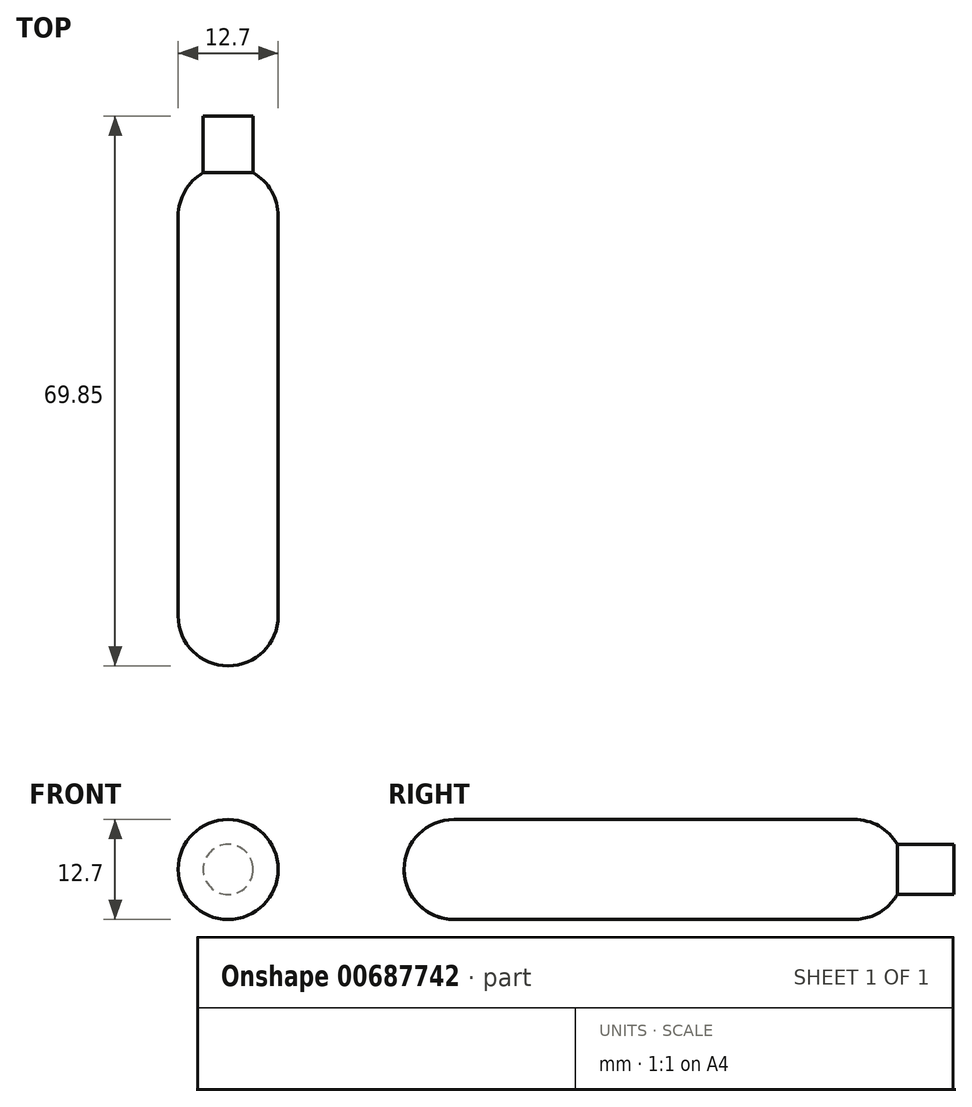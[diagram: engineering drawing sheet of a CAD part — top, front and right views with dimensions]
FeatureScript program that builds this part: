
annotation { "Feature Type Name" : "Feature", "Feature Type Description" : "" }
export const myFeature = defineFeature(function(context is Context, id is Id, definition is map)
    precondition{}
    {
        {
            var Q0;
            Q0=qCreatedBy(makeId("Front.planeOp"),FACE);
            var sketch = newSketch(context, id + "F0", { "sketchPlane" : qUnion([Q0])});
            skCircle(sketch, "E0", {"center": v(0, 0) * mm, "radius": 6.35 * mm});
            skSolve(sketch);
        }
        {
            var Q0;
            Q0=makeQuery(id+"F0.imprint","IMPRINT",FACE,{"disambiguationData":[TD([[makeQuery(id+"F0.imprint","IMPRINT",EDGE,{"derivedFrom":sQuery(id+"F0.wireOp",EDGE,"E0")}),1.0]])]});
            extrude(context, id + "F1", {"entities" : qUnion([Q0]), "depth" : 63.5 * mm, "offsetDistance" : 25.4 * mm});
        }
        {
            var Q0;
            Q0=makeQuery(id+"F1.opExtrude","CAP_FACE",FACE,{"disambiguationData":[OSD([sQuery(id+"F0.wireOp",EDGE,"E0")])],"isStart":false});
            var Q1;
            Q1=makeQuery(id+"F1.opExtrude","CAP_FACE",FACE,{"disambiguationData":[OSD([sQuery(id+"F0.wireOp",EDGE,"E0")])],"isStart":true});
            fillet(context, id + "F2", {"entities" : qUnion([Q0, Q1]), "radius" : 6.35 * mm, "tangentPropagation" : true, "allowEdgeOverflow" : false});
        }
        {
            var Q0;
            Q0=qCreatedBy(makeId("Front.planeOp"),FACE);
            var sketch = newSketch(context, id + "F3", { "sketchPlane" : qUnion([Q0])});
            skCircle(sketch, "E1", {"center": v(0, 0) * mm, "radius": 3.18 * mm});
            skSolve(sketch);
        }
        {
            var Q0;
            Q0 = qSketchRegion(id + "F3", true);
            extrude(context, id + "F4", {"entities" : qUnion([Q0]), "operationType" : NewBodyOperationType.ADD, "endBound" : BoundingType.SYMMETRIC, "depth" : 12.7 * mm, "offsetDistance" : 25.4 * mm});
        }
    });
